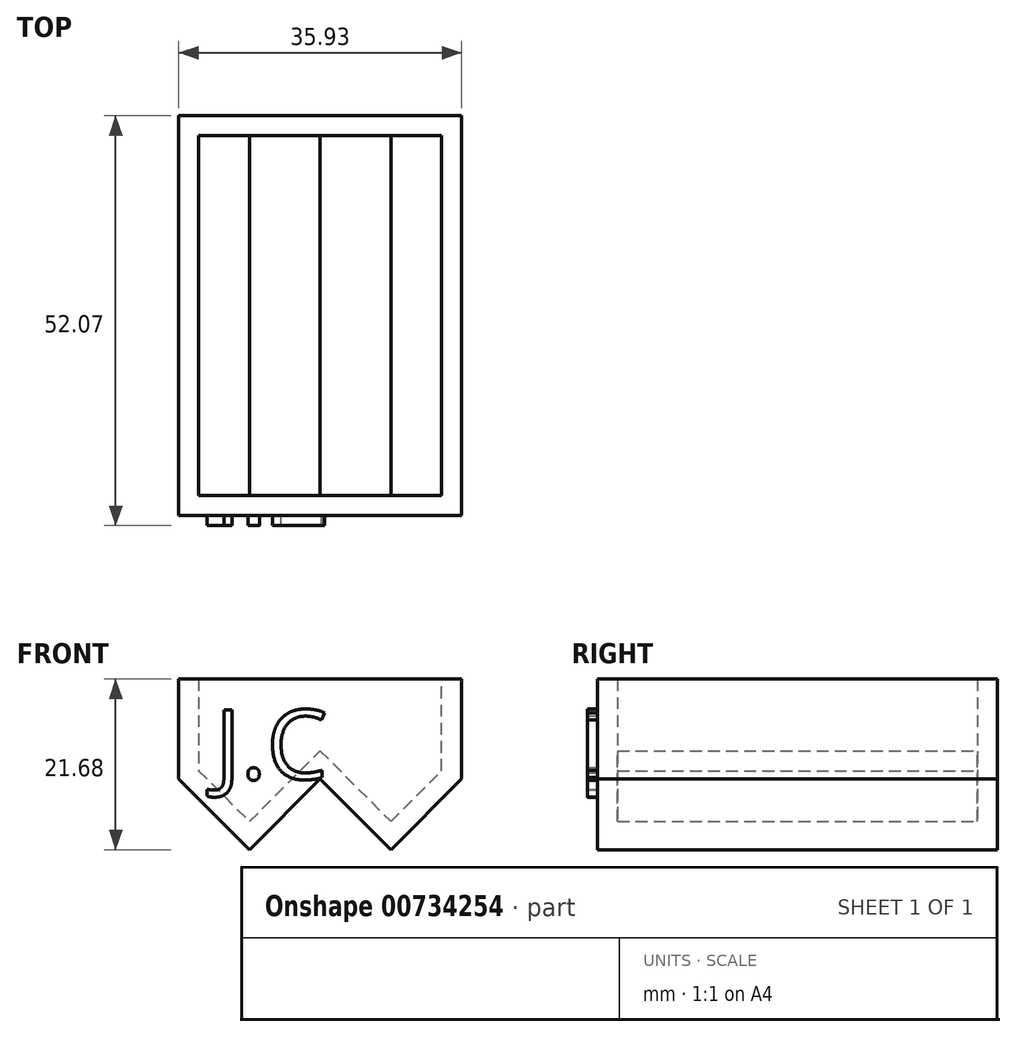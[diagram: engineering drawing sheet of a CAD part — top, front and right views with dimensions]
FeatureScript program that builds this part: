
annotation { "Feature Type Name" : "Feature", "Feature Type Description" : "" }
export const myFeature = defineFeature(function(context is Context, id is Id, definition is map)
    precondition{}
    {
        {
            var Q0;
            Q0=qCreatedBy(makeId("Front.planeOp"),FACE);
            var sketch = newSketch(context, id + "F0", { "sketchPlane" : qUnion([Q0])});
            skLineSegment(sketch, "E0", {"start": v(-42.3, 17.74) * mm, "end": v(-42.3, 5.04) * mm});
            skLineSegment(sketch, "E1", {"start": v(-42.3, 5.04) * mm, "end": v(-33.32, -3.94) * mm});
            skLineSegment(sketch, "E2", {"start": v(-33.32, -3.94) * mm, "end": v(-24.33, 5.04) * mm});
            skLineSegment(sketch, "E3", {"start": v(-24.33, 5.04) * mm, "end": v(-15.35, -3.94) * mm});
            skLineSegment(sketch, "E4", {"start": v(-15.35, -3.94) * mm, "end": v(-6.37, 5.04) * mm});
            skLineSegment(sketch, "E5", {"start": v(-6.37, 5.04) * mm, "end": v(-6.37, 17.74) * mm});
            skLineSegment(sketch, "E6", {"start": v(-6.37, 17.74) * mm, "end": v(-42.3, 17.74) * mm});
            skSolve(sketch);
        }
        {
            var Q0;
            Q0=makeQuery(id+"F0.imprint","IMPRINT",FACE,{"disambiguationData":[TD([[makeQuery(id+"F0.imprint","IMPRINT",EDGE,{"derivedFrom":sQuery(id+"F0.wireOp",EDGE,"E0")}),1.0]])]});
            extrude(context, id + "F1", {"entities" : qUnion([Q0]), "depth" : 50.8 * mm, "offsetDistance" : 25.4 * mm});
        }
        {
            var Q0;
            Q0=makeQuery(id+"F1.opExtrude","SWEPT_FACE",FACE,{"disambiguationData":[OSD([sQuery(id+"F0.wireOp",EDGE,"E6")])]});
            shell(context, id + "F2", {"entities" : qUnion([Q0]), "thickness" : 2.54 * mm});
        }
        {
            var Q0;
            Q0=makeQuery(id+"F1.opExtrude","CAP_FACE",FACE,{"disambiguationData":[OSD([sQuery(id+"F0.wireOp",EDGE,"E0"),sQuery(id+"F0.wireOp",EDGE,"E1"),sQuery(id+"F0.wireOp",EDGE,"E2"),sQuery(id+"F0.wireOp",EDGE,"E3"),sQuery(id+"F0.wireOp",EDGE,"E4"),sQuery(id+"F0.wireOp",EDGE,"E5"),sQuery(id+"F0.wireOp",EDGE,"E6")])],"isStart":false});
            var sketch = newSketch(context, id + "F3", { "sketchPlane" : qUnion([Q0])});
            skText(sketch, "E7", { "text": "J.C", "fontName": "OpenSans-Regular.ttf"});
            const initialGuessF3  = {"E7": [-0.03771, 0.00504, 1, 0, 0.00886]};
            skSetInitialGuess(sketch, initialGuessF3);
            skSolve(sketch);
        }
        {
            var Q0;
            Q0 = qSketchRegion(id + "F3", true);
            extrude(context, id + "F4", {"entities" : qUnion([Q0]), "operationType" : NewBodyOperationType.ADD, "depth" : 1.27 * mm, "offsetDistance" : 25.4 * mm});
        }
    });
